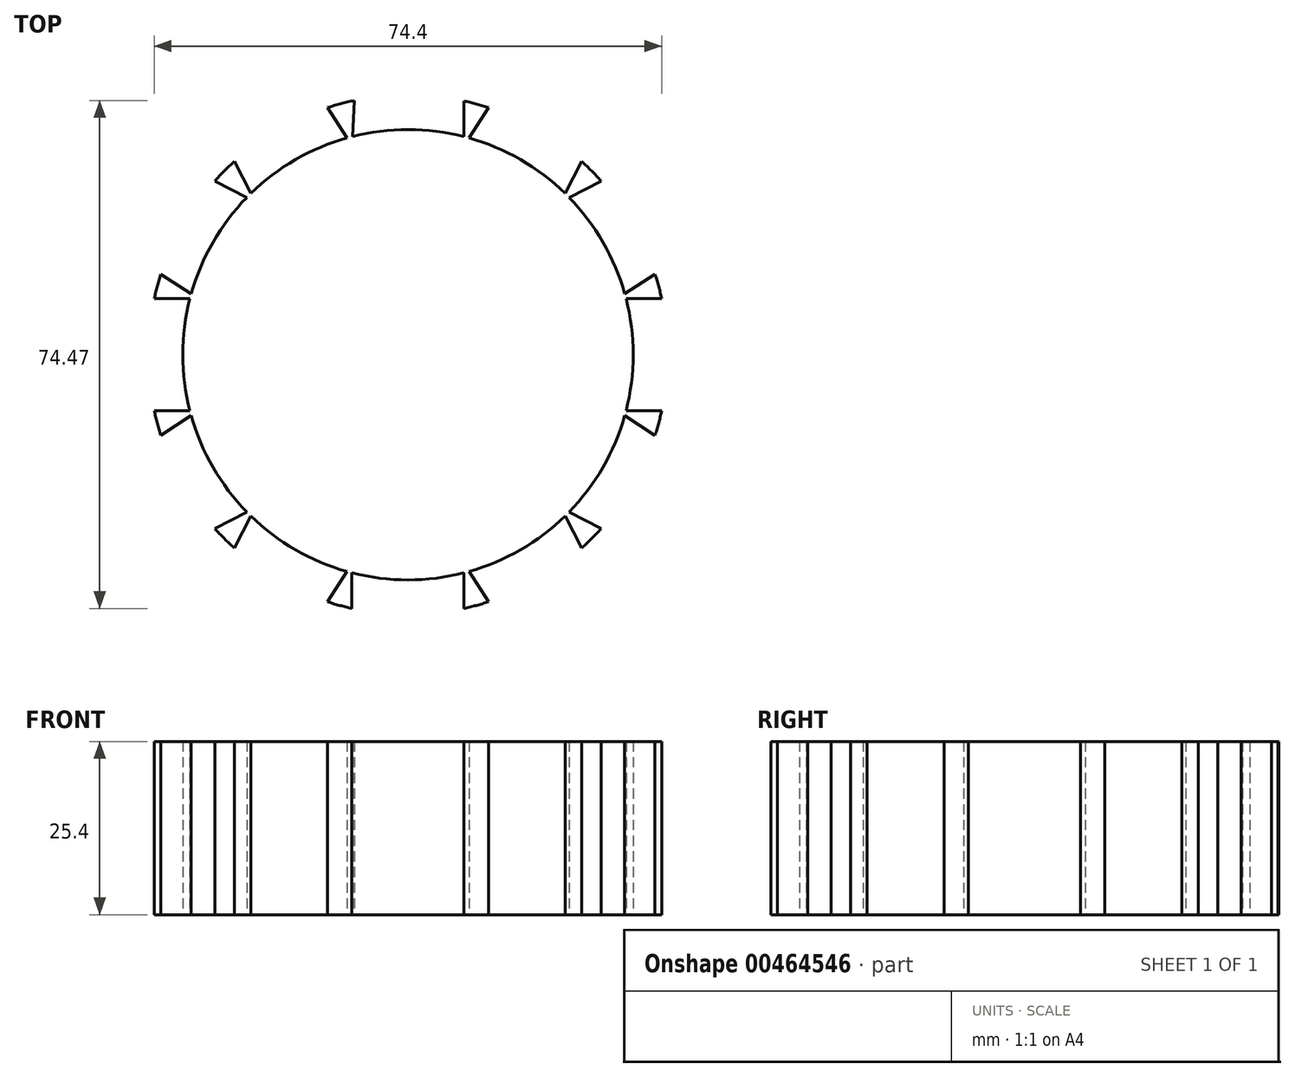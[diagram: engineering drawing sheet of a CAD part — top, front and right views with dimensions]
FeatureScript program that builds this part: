
annotation { "Feature Type Name" : "Feature", "Feature Type Description" : "" }
export const myFeature = defineFeature(function(context is Context, id is Id, definition is map)
    precondition{}
    {
        {
            var Q0;
            Q0=qCreatedBy(makeId("Top.planeOp"),FACE);
            var sketch = newSketch(context, id + "F0", { "sketchPlane" : qUnion([Q0])});
            skCircle(sketch, "E0", {"center": v(0, 0) * mm, "radius": 38.1 * mm});
            skCircle(sketch, "E1", {"center": v(0, 0) * mm, "radius": 31.75 * mm});
            skCircle(sketch, "E2.cCircle", {"center": v(0, 0) * mm, "radius": 38.1 * mm, "construction": true});
            skPoint(sketch, "E2.0.midPoint", {"position": v(0, -38.1) * mm});
            skCircle(sketch, "E3.cCircle", {"center": v(0, 0) * mm, "radius": 31.75 * mm, "construction": true});
            skLineSegment(sketch, "E4", {"start": v(30.67, 8.22) * mm, "end": v(37.2, 8.22) * mm});
            skLineSegment(sketch, "E5", {"start": v(30.67, -8.22) * mm, "end": v(37.2, -8.22) * mm});
            skLineSegment(sketch, "E6", {"start": v(30.67, -8.22) * mm, "end": v(36.22, -11.8) * mm});
            skLineSegment(sketch, "E7", {"start": v(22.45, -22.45) * mm, "end": v(28.34, -25.47) * mm});
            skLineSegment(sketch, "E8", {"start": v(8.22, -30.67) * mm, "end": v(11.8, -36.22) * mm});
            skLineSegment(sketch, "E9", {"start": v(8.22, -30.67) * mm, "end": v(8.22, -37.2) * mm});
            skLineSegment(sketch, "E10", {"start": v(-8.22, -30.67) * mm, "end": v(-8.22, -37.2) * mm});
            skLineSegment(sketch, "E11", {"start": v(-8.22, -30.67) * mm, "end": v(-11.8, -36.22) * mm});
            skLineSegment(sketch, "E12", {"start": v(-22.45, -22.45) * mm, "end": v(-25.47, -28.34) * mm});
            skLineSegment(sketch, "E13", {"start": v(-22.45, -22.45) * mm, "end": v(-28.34, -25.47) * mm});
            skLineSegment(sketch, "E14", {"start": v(-30.67, -8.22) * mm, "end": v(-36.22, -11.8) * mm});
            skLineSegment(sketch, "E15", {"start": v(-30.67, -8.22) * mm, "end": v(-37.2, -8.22) * mm});
            skLineSegment(sketch, "E16", {"start": v(30.67, 8.22) * mm, "end": v(36.22, 11.8) * mm});
            skLineSegment(sketch, "E17", {"start": v(22.45, 22.45) * mm, "end": v(28.34, 25.47) * mm});
            skLineSegment(sketch, "E18", {"start": v(22.45, 22.45) * mm, "end": v(25.47, 28.34) * mm});
            skLineSegment(sketch, "E19", {"start": v(8.22, 30.67) * mm, "end": v(11.8, 36.22) * mm});
            skLineSegment(sketch, "E20", {"start": v(8.22, 30.67) * mm, "end": v(8.22, 37.2) * mm});
            skLineSegment(sketch, "E21", {"start": v(-8.22, 30.67) * mm, "end": v(-7.89, 37.27) * mm});
            skLineSegment(sketch, "E22", {"start": v(-8.22, 30.67) * mm, "end": v(-11.8, 36.22) * mm});
            skLineSegment(sketch, "E23", {"start": v(-22.45, 22.45) * mm, "end": v(-25.47, 28.34) * mm});
            skLineSegment(sketch, "E24", {"start": v(-22.45, 22.45) * mm, "end": v(-28.34, 25.47) * mm});
            skLineSegment(sketch, "E25", {"start": v(-30.67, 8.22) * mm, "end": v(-36.22, 11.8) * mm});
            skLineSegment(sketch, "E26", {"start": v(-30.67, 8.22) * mm, "end": v(-37.2, 8.22) * mm});
            skCircle(sketch, "E27", {"center": v(0, 0) * mm, "radius": 33.02 * mm});
            skLineSegment(sketch, "E28", {"start": v(22.45, -22.45) * mm, "end": v(25.47, -28.34) * mm});
            skSolve(sketch);
        }
        {
            var Q0;
            {var subQ1=sQuery(id+"F0.wireOp",EDGE,"E19");var subQ3=sQuery(id+"F0.wireOp",EDGE,"E27");var subQ4=makeQuery(id+"F0.imprint","INTERSECT",VERTEX,{"derivedFrom":[subQ1,subQ3]});Q0=makeQuery(id+"F0.imprint","IMPRINT",FACE,{"disambiguationData":[TD([[makeQuery(id+"F0.imprint","IMPRINT",EDGE,{"disambiguationData":[TD([[subQ4,-1.0]])],"derivedFrom":subQ3}),1.0]])]});}
            var Q1;
            {var subQ0=sQuery(id+"F0.wireOp",EDGE,"E20");var subQ5=sQuery(id+"F0.wireOp",EDGE,"E27");var subQ6=makeQuery(id+"F0.imprint","INTERSECT",VERTEX,{"derivedFrom":[subQ0,subQ5]});Q1=makeQuery(id+"F0.imprint","IMPRINT",FACE,{"disambiguationData":[TD([[makeQuery(id+"F0.imprint","IMPRINT",EDGE,{"disambiguationData":[TD([[subQ6,-1.0]])],"derivedFrom":subQ5}),1.0]])]});}
            var Q2;
            {var subQ0=sQuery(id+"F0.wireOp",EDGE,"E19");var subQ1=sQuery(id+"F0.wireOp",EDGE,"E0");var subQ2=makeQuery(id+"F0.imprint","INTERSECT",VERTEX,{"derivedFrom":[subQ1,subQ0]});Q2=makeQuery(id+"F0.imprint","IMPRINT",FACE,{"disambiguationData":[TD([[makeQuery(id+"F0.imprint","IMPRINT",EDGE,{"disambiguationData":[TD([[subQ2,-1.0]])],"derivedFrom":subQ1}),1.0]])]});}
            var Q3;
            {var subQ0=sQuery(id+"F0.wireOp",EDGE,"E18");var subQ5=sQuery(id+"F0.wireOp",EDGE,"E27");var subQ6=makeQuery(id+"F0.imprint","INTERSECT",VERTEX,{"derivedFrom":[subQ0,subQ5]});Q3=makeQuery(id+"F0.imprint","IMPRINT",FACE,{"disambiguationData":[TD([[makeQuery(id+"F0.imprint","IMPRINT",EDGE,{"disambiguationData":[TD([[subQ6,-1.0]])],"derivedFrom":subQ5}),1.0]])]});}
            var Q4;
            {var subQ0=sQuery(id+"F0.wireOp",EDGE,"E17");var subQ1=sQuery(id+"F0.wireOp",EDGE,"E0");var subQ2=makeQuery(id+"F0.imprint","INTERSECT",VERTEX,{"derivedFrom":[subQ1,subQ0]});Q4=makeQuery(id+"F0.imprint","IMPRINT",FACE,{"disambiguationData":[TD([[makeQuery(id+"F0.imprint","IMPRINT",EDGE,{"disambiguationData":[TD([[subQ2,-1.0]])],"derivedFrom":subQ1}),1.0]])]});}
            var Q5;
            {var subQ1=sQuery(id+"F0.wireOp",EDGE,"E17");var subQ3=sQuery(id+"F0.wireOp",EDGE,"E27");var subQ4=makeQuery(id+"F0.imprint","INTERSECT",VERTEX,{"derivedFrom":[subQ1,subQ3]});Q5=makeQuery(id+"F0.imprint","IMPRINT",FACE,{"disambiguationData":[TD([[makeQuery(id+"F0.imprint","IMPRINT",EDGE,{"disambiguationData":[TD([[subQ4,-1.0]])],"derivedFrom":subQ3}),1.0]])]});}
            var Q6;
            {var subQ0=sQuery(id+"F0.wireOp",EDGE,"E16");var subQ5=sQuery(id+"F0.wireOp",EDGE,"E27");var subQ7=makeQuery(id+"F0.imprint","INTERSECT",VERTEX,{"derivedFrom":[subQ0,subQ5]});Q6=makeQuery(id+"F0.imprint","IMPRINT",FACE,{"disambiguationData":[TD([[makeQuery(id+"F0.imprint","IMPRINT",EDGE,{"disambiguationData":[TD([[subQ7,-1.0]])],"derivedFrom":subQ5}),1.0]])]});}
            var Q7;
            {var subQ1=sQuery(id+"F0.wireOp",EDGE,"E4");var subQ3=sQuery(id+"F0.wireOp",EDGE,"E27");var subQ4=makeQuery(id+"F0.imprint","INTERSECT",VERTEX,{"derivedFrom":[subQ1,subQ3]});Q7=makeQuery(id+"F0.imprint","IMPRINT",FACE,{"disambiguationData":[TD([[makeQuery(id+"F0.imprint","IMPRINT",EDGE,{"disambiguationData":[TD([[subQ4,-1.0]])],"derivedFrom":subQ3}),1.0]])]});}
            var Q8;
            {var subQ0=sQuery(id+"F0.wireOp",EDGE,"E4");var subQ1=sQuery(id+"F0.wireOp",EDGE,"E0");var subQ2=makeQuery(id+"F0.imprint","INTERSECT",VERTEX,{"derivedFrom":[subQ1,subQ0]});Q8=makeQuery(id+"F0.imprint","IMPRINT",FACE,{"disambiguationData":[TD([[makeQuery(id+"F0.imprint","IMPRINT",EDGE,{"disambiguationData":[TD([[subQ2,-1.0]])],"derivedFrom":subQ1}),1.0]])]});}
            var Q9;
            {var subQ0=sQuery(id+"F0.wireOp",EDGE,"E4");var subQ5=sQuery(id+"F0.wireOp",EDGE,"E27");var subQ7=makeQuery(id+"F0.imprint","INTERSECT",VERTEX,{"derivedFrom":[subQ0,subQ5]});Q9=makeQuery(id+"F0.imprint","IMPRINT",FACE,{"disambiguationData":[TD([[makeQuery(id+"F0.imprint","IMPRINT",EDGE,{"disambiguationData":[TD([[subQ7,1.0]])],"derivedFrom":subQ5}),1.0]])]});}
            var Q10;
            {var subQ1=sQuery(id+"F0.wireOp",EDGE,"E5");var subQ3=sQuery(id+"F0.wireOp",EDGE,"E27");var subQ4=makeQuery(id+"F0.imprint","INTERSECT",VERTEX,{"derivedFrom":[subQ1,subQ3]});Q10=makeQuery(id+"F0.imprint","IMPRINT",FACE,{"disambiguationData":[TD([[makeQuery(id+"F0.imprint","IMPRINT",EDGE,{"disambiguationData":[TD([[subQ4,1.0]])],"derivedFrom":subQ3}),1.0]])]});}
            var Q11;
            {var subQ0=sQuery(id+"F0.wireOp",EDGE,"E5");var subQ1=sQuery(id+"F0.wireOp",EDGE,"E0");var subQ2=makeQuery(id+"F0.imprint","INTERSECT",VERTEX,{"derivedFrom":[subQ1,subQ0]});Q11=makeQuery(id+"F0.imprint","IMPRINT",FACE,{"disambiguationData":[TD([[makeQuery(id+"F0.imprint","IMPRINT",EDGE,{"disambiguationData":[TD([[subQ2,1.0]])],"derivedFrom":subQ1}),1.0]])]});}
            var Q12;
            {var subQ3=sQuery(id+"F0.wireOp",EDGE,"E6");var subQ5=sQuery(id+"F0.wireOp",EDGE,"E27");var subQ7=makeQuery(id+"F0.imprint","INTERSECT",VERTEX,{"derivedFrom":[subQ3,subQ5]});Q12=makeQuery(id+"F0.imprint","IMPRINT",FACE,{"disambiguationData":[TD([[makeQuery(id+"F0.imprint","IMPRINT",EDGE,{"disambiguationData":[TD([[subQ7,1.0]])],"derivedFrom":subQ5}),1.0]])]});}
            var Q13;
            {var subQ0=sQuery(id+"F0.wireOp",EDGE,"HboYdi5V-8zPe-B9Os-IQrA-6UwbVvCPj5eX");var subQ5=sQuery(id+"F0.wireOp",EDGE,"E27");var subQ6=makeQuery(id+"F0.imprint","INTERSECT",VERTEX,{"derivedFrom":[subQ0,subQ5]});Q13=makeQuery(id+"F0.imprint","IMPRINT",FACE,{"disambiguationData":[TD([[makeQuery(id+"F0.imprint","IMPRINT",EDGE,{"disambiguationData":[TD([[subQ6,1.0]])],"derivedFrom":subQ5}),1.0]])]});}
            var Q14;
            {var subQ1=sQuery(id+"F0.wireOp",EDGE,"HboYdi5V-8zPe-B9Os-IQrA-6UwbVvCPj5eX");var subQ3=sQuery(id+"F0.wireOp",EDGE,"E27");var subQ4=makeQuery(id+"F0.imprint","INTERSECT",VERTEX,{"derivedFrom":[subQ1,subQ3]});Q14=makeQuery(id+"F0.imprint","IMPRINT",FACE,{"disambiguationData":[TD([[makeQuery(id+"F0.imprint","IMPRINT",EDGE,{"disambiguationData":[TD([[subQ4,-1.0]])],"derivedFrom":subQ3}),1.0]])]});}
            var Q15;
            {var subQ1=sQuery(id+"F0.wireOp",EDGE,"E8");var subQ3=sQuery(id+"F0.wireOp",EDGE,"E27");var subQ4=makeQuery(id+"F0.imprint","INTERSECT",VERTEX,{"derivedFrom":[subQ1,subQ3]});Q15=makeQuery(id+"F0.imprint","IMPRINT",FACE,{"disambiguationData":[TD([[makeQuery(id+"F0.imprint","IMPRINT",EDGE,{"disambiguationData":[TD([[subQ4,1.0]])],"derivedFrom":subQ3}),1.0]])]});}
            var Q16;
            {var subQ0=sQuery(id+"F0.wireOp",EDGE,"E9");var subQ5=sQuery(id+"F0.wireOp",EDGE,"E27");var subQ6=makeQuery(id+"F0.imprint","INTERSECT",VERTEX,{"derivedFrom":[subQ0,subQ5]});Q16=makeQuery(id+"F0.imprint","IMPRINT",FACE,{"disambiguationData":[TD([[makeQuery(id+"F0.imprint","IMPRINT",EDGE,{"disambiguationData":[TD([[subQ6,1.0]])],"derivedFrom":subQ5}),1.0]])]});}
            var Q17;
            {var subQ1=sQuery(id+"F0.wireOp",EDGE,"E10");var subQ3=sQuery(id+"F0.wireOp",EDGE,"E27");var subQ4=makeQuery(id+"F0.imprint","INTERSECT",VERTEX,{"derivedFrom":[subQ1,subQ3]});Q17=makeQuery(id+"F0.imprint","IMPRINT",FACE,{"disambiguationData":[TD([[makeQuery(id+"F0.imprint","IMPRINT",EDGE,{"disambiguationData":[TD([[subQ4,1.0]])],"derivedFrom":subQ3}),1.0]])]});}
            var Q18;
            {var subQ0=sQuery(id+"F0.wireOp",EDGE,"E11");var subQ5=sQuery(id+"F0.wireOp",EDGE,"E27");var subQ6=makeQuery(id+"F0.imprint","INTERSECT",VERTEX,{"derivedFrom":[subQ0,subQ5]});Q18=makeQuery(id+"F0.imprint","IMPRINT",FACE,{"disambiguationData":[TD([[makeQuery(id+"F0.imprint","IMPRINT",EDGE,{"disambiguationData":[TD([[subQ6,1.0]])],"derivedFrom":subQ5}),1.0]])]});}
            var Q19;
            {var subQ1=sQuery(id+"F0.wireOp",EDGE,"E12");var subQ3=sQuery(id+"F0.wireOp",EDGE,"E27");var subQ4=makeQuery(id+"F0.imprint","INTERSECT",VERTEX,{"derivedFrom":[subQ1,subQ3]});Q19=makeQuery(id+"F0.imprint","IMPRINT",FACE,{"disambiguationData":[TD([[makeQuery(id+"F0.imprint","IMPRINT",EDGE,{"disambiguationData":[TD([[subQ4,1.0]])],"derivedFrom":subQ3}),1.0]])]});}
            var Q20;
            {var subQ0=sQuery(id+"F0.wireOp",EDGE,"E13");var subQ5=sQuery(id+"F0.wireOp",EDGE,"E27");var subQ6=makeQuery(id+"F0.imprint","INTERSECT",VERTEX,{"derivedFrom":[subQ0,subQ5]});Q20=makeQuery(id+"F0.imprint","IMPRINT",FACE,{"disambiguationData":[TD([[makeQuery(id+"F0.imprint","IMPRINT",EDGE,{"disambiguationData":[TD([[subQ6,1.0]])],"derivedFrom":subQ5}),1.0]])]});}
            var Q21;
            {var subQ1=sQuery(id+"F0.wireOp",EDGE,"E14");var subQ3=sQuery(id+"F0.wireOp",EDGE,"E27");var subQ4=makeQuery(id+"F0.imprint","INTERSECT",VERTEX,{"derivedFrom":[subQ1,subQ3]});Q21=makeQuery(id+"F0.imprint","IMPRINT",FACE,{"disambiguationData":[TD([[makeQuery(id+"F0.imprint","IMPRINT",EDGE,{"disambiguationData":[TD([[subQ4,1.0]])],"derivedFrom":subQ3}),1.0]])]});}
            var Q22;
            {var subQ0=sQuery(id+"F0.wireOp",EDGE,"E15");var subQ5=sQuery(id+"F0.wireOp",EDGE,"E27");var subQ6=makeQuery(id+"F0.imprint","INTERSECT",VERTEX,{"derivedFrom":[subQ0,subQ5]});Q22=makeQuery(id+"F0.imprint","IMPRINT",FACE,{"disambiguationData":[TD([[makeQuery(id+"F0.imprint","IMPRINT",EDGE,{"disambiguationData":[TD([[subQ6,1.0]])],"derivedFrom":subQ5}),1.0]])]});}
            var Q23;
            {var subQ1=sQuery(id+"F0.wireOp",EDGE,"E25");var subQ3=sQuery(id+"F0.wireOp",EDGE,"E27");var subQ4=makeQuery(id+"F0.imprint","INTERSECT",VERTEX,{"derivedFrom":[subQ1,subQ3]});Q23=makeQuery(id+"F0.imprint","IMPRINT",FACE,{"disambiguationData":[TD([[makeQuery(id+"F0.imprint","IMPRINT",EDGE,{"disambiguationData":[TD([[subQ4,-1.0]])],"derivedFrom":subQ3}),1.0]])]});}
            var Q24;
            {var subQ0=sQuery(id+"F0.wireOp",EDGE,"E24");var subQ5=sQuery(id+"F0.wireOp",EDGE,"E27");var subQ6=makeQuery(id+"F0.imprint","INTERSECT",VERTEX,{"derivedFrom":[subQ0,subQ5]});Q24=makeQuery(id+"F0.imprint","IMPRINT",FACE,{"disambiguationData":[TD([[makeQuery(id+"F0.imprint","IMPRINT",EDGE,{"disambiguationData":[TD([[subQ6,-1.0]])],"derivedFrom":subQ5}),1.0]])]});}
            var Q25;
            {var subQ1=sQuery(id+"F0.wireOp",EDGE,"E23");var subQ3=sQuery(id+"F0.wireOp",EDGE,"E27");var subQ4=makeQuery(id+"F0.imprint","INTERSECT",VERTEX,{"derivedFrom":[subQ1,subQ3]});Q25=makeQuery(id+"F0.imprint","IMPRINT",FACE,{"disambiguationData":[TD([[makeQuery(id+"F0.imprint","IMPRINT",EDGE,{"disambiguationData":[TD([[subQ4,-1.0]])],"derivedFrom":subQ3}),1.0]])]});}
            var Q26;
            {var subQ0=sQuery(id+"F0.wireOp",EDGE,"E22");var subQ5=sQuery(id+"F0.wireOp",EDGE,"E27");var subQ6=makeQuery(id+"F0.imprint","INTERSECT",VERTEX,{"derivedFrom":[subQ0,subQ5]});Q26=makeQuery(id+"F0.imprint","IMPRINT",FACE,{"disambiguationData":[TD([[makeQuery(id+"F0.imprint","IMPRINT",EDGE,{"disambiguationData":[TD([[subQ6,-1.0]])],"derivedFrom":subQ5}),1.0]])]});}
            var Q27;
            {var subQ1=sQuery(id+"F0.wireOp",EDGE,"E21");var subQ3=sQuery(id+"F0.wireOp",EDGE,"E27");var subQ4=makeQuery(id+"F0.imprint","INTERSECT",VERTEX,{"derivedFrom":[subQ1,subQ3]});Q27=makeQuery(id+"F0.imprint","IMPRINT",FACE,{"disambiguationData":[TD([[makeQuery(id+"F0.imprint","IMPRINT",EDGE,{"disambiguationData":[TD([[subQ4,-1.0]])],"derivedFrom":subQ3}),1.0]])]});}
            var Q28;
            {var subQ0=sQuery(id+"F0.wireOp",EDGE,"E7");var subQ1=sQuery(id+"F0.wireOp",EDGE,"E0");var subQ2=makeQuery(id+"F0.imprint","INTERSECT",VERTEX,{"derivedFrom":[subQ1,subQ0]});Q28=makeQuery(id+"F0.imprint","IMPRINT",FACE,{"disambiguationData":[TD([[makeQuery(id+"F0.imprint","IMPRINT",EDGE,{"disambiguationData":[TD([[subQ2,1.0]])],"derivedFrom":subQ1}),1.0]])]});}
            var Q29;
            {var subQ0=sQuery(id+"F0.wireOp",EDGE,"E8");var subQ1=sQuery(id+"F0.wireOp",EDGE,"E0");var subQ2=makeQuery(id+"F0.imprint","INTERSECT",VERTEX,{"derivedFrom":[subQ1,subQ0]});Q29=makeQuery(id+"F0.imprint","IMPRINT",FACE,{"disambiguationData":[TD([[makeQuery(id+"F0.imprint","IMPRINT",EDGE,{"disambiguationData":[TD([[subQ2,1.0]])],"derivedFrom":subQ1}),1.0]])]});}
            var Q30;
            {var subQ0=sQuery(id+"F0.wireOp",EDGE,"E10");var subQ1=sQuery(id+"F0.wireOp",EDGE,"E0");var subQ2=makeQuery(id+"F0.imprint","INTERSECT",VERTEX,{"derivedFrom":[subQ1,subQ0]});Q30=makeQuery(id+"F0.imprint","IMPRINT",FACE,{"disambiguationData":[TD([[makeQuery(id+"F0.imprint","IMPRINT",EDGE,{"disambiguationData":[TD([[subQ2,1.0]])],"derivedFrom":subQ1}),1.0]])]});}
            var Q31;
            {var subQ0=sQuery(id+"F0.wireOp",EDGE,"E12");var subQ1=sQuery(id+"F0.wireOp",EDGE,"E0");var subQ2=makeQuery(id+"F0.imprint","INTERSECT",VERTEX,{"derivedFrom":[subQ1,subQ0]});Q31=makeQuery(id+"F0.imprint","IMPRINT",FACE,{"disambiguationData":[TD([[makeQuery(id+"F0.imprint","IMPRINT",EDGE,{"disambiguationData":[TD([[subQ2,1.0]])],"derivedFrom":subQ1}),1.0]])]});}
            var Q32;
            {var subQ0=sQuery(id+"F0.wireOp",EDGE,"E14");var subQ1=sQuery(id+"F0.wireOp",EDGE,"E0");var subQ2=makeQuery(id+"F0.imprint","INTERSECT",VERTEX,{"derivedFrom":[subQ1,subQ0]});Q32=makeQuery(id+"F0.imprint","IMPRINT",FACE,{"disambiguationData":[TD([[makeQuery(id+"F0.imprint","IMPRINT",EDGE,{"disambiguationData":[TD([[subQ2,1.0]])],"derivedFrom":subQ1}),1.0]])]});}
            var Q33;
            {var subQ0=sQuery(id+"F0.wireOp",EDGE,"E25");var subQ1=sQuery(id+"F0.wireOp",EDGE,"E0");var subQ2=makeQuery(id+"F0.imprint","INTERSECT",VERTEX,{"derivedFrom":[subQ1,subQ0]});Q33=makeQuery(id+"F0.imprint","IMPRINT",FACE,{"disambiguationData":[TD([[makeQuery(id+"F0.imprint","IMPRINT",EDGE,{"disambiguationData":[TD([[subQ2,-1.0]])],"derivedFrom":subQ1}),1.0]])]});}
            var Q34;
            {var subQ0=sQuery(id+"F0.wireOp",EDGE,"E23");var subQ1=sQuery(id+"F0.wireOp",EDGE,"E0");var subQ2=makeQuery(id+"F0.imprint","INTERSECT",VERTEX,{"derivedFrom":[subQ1,subQ0]});Q34=makeQuery(id+"F0.imprint","IMPRINT",FACE,{"disambiguationData":[TD([[makeQuery(id+"F0.imprint","IMPRINT",EDGE,{"disambiguationData":[TD([[subQ2,-1.0]])],"derivedFrom":subQ1}),1.0]])]});}
            var Q35;
            {var subQ0=sQuery(id+"F0.wireOp",EDGE,"E21");var subQ1=sQuery(id+"F0.wireOp",EDGE,"E0");var subQ2=makeQuery(id+"F0.imprint","INTERSECT",VERTEX,{"derivedFrom":[subQ1,subQ0]});Q35=makeQuery(id+"F0.imprint","IMPRINT",FACE,{"disambiguationData":[TD([[makeQuery(id+"F0.imprint","IMPRINT",EDGE,{"disambiguationData":[TD([[subQ2,-1.0]])],"derivedFrom":subQ1}),1.0]])]});}
            var Q36;
            {var subQ0=sQuery(id+"F0.wireOp",EDGE,"E1");var subQ8=makeQuery(id+"F0.imprint","INTERSECT",VERTEX,{"derivedFrom":[subQ0,sQuery(id+"F0.wireOp",EDGE,"E4"),sQuery(id+"F0.wireOp",EDGE,"E16")]});Q36=makeQuery(id+"F0.imprint","IMPRINT",FACE,{"disambiguationData":[TD([[makeQuery(id+"F0.imprint","IMPRINT",EDGE,{"disambiguationData":[TD([[subQ8,-1.0]])],"derivedFrom":subQ0}),1.0]])]});}
            var Q37;
            {var subQ3=sQuery(id+"F0.wireOp",EDGE,"E8");var subQ5=sQuery(id+"F0.wireOp",EDGE,"E27");var subQ6=makeQuery(id+"F0.imprint","INTERSECT",VERTEX,{"derivedFrom":[subQ3,subQ5]});Q37=makeQuery(id+"F0.imprint","IMPRINT",FACE,{"disambiguationData":[TD([[makeQuery(id+"F0.imprint","IMPRINT",EDGE,{"disambiguationData":[TD([[subQ6,-1.0]])],"derivedFrom":subQ5}),1.0]])]});}
            extrude(context, id + "F1", {"entities" : qUnion([Q0, Q1, Q2, Q3, Q4, Q5, Q6, Q7, Q8, Q9, Q10, Q11, Q12, Q13, Q14, Q15, Q16, Q17, Q18, Q19, Q20, Q21, Q22, Q23, Q24, Q25, Q26, Q27, Q28, Q29, Q30, Q31, Q32, Q33, Q34, Q35, Q36, Q37]), "depth" : 25.4 * mm});
        }
    });
